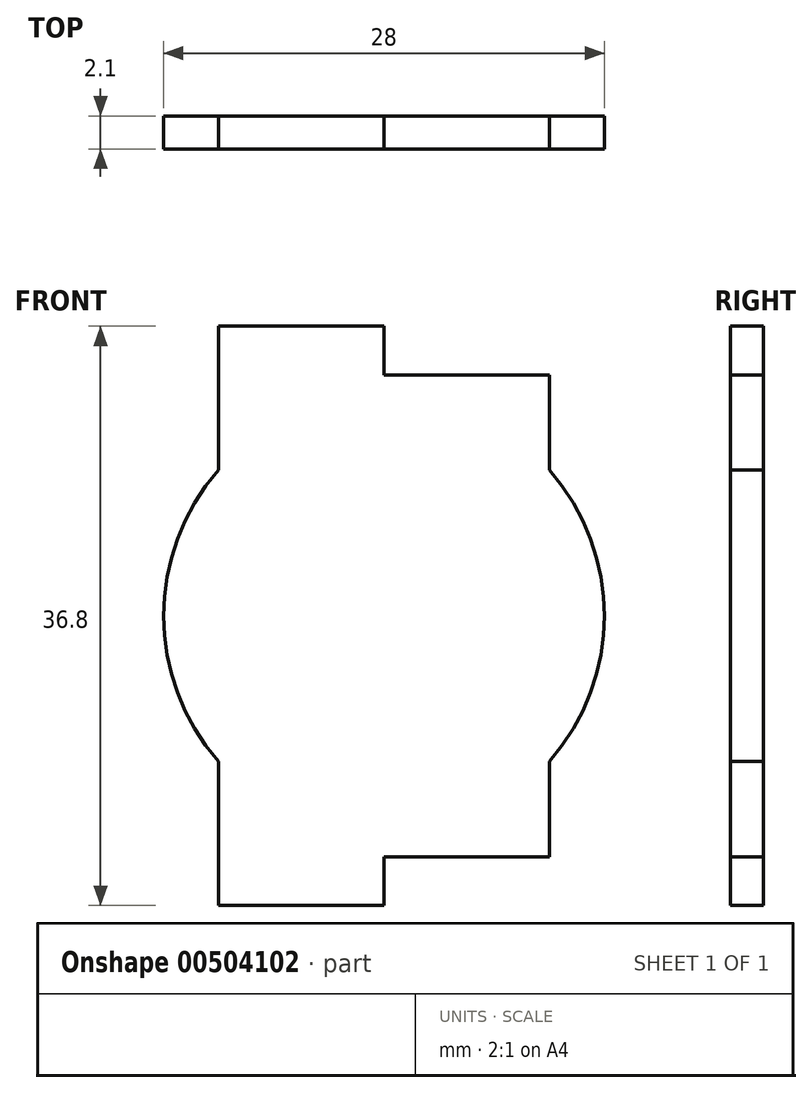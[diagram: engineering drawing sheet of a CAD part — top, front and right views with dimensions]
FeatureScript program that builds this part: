
annotation { "Feature Type Name" : "Feature", "Feature Type Description" : "" }
export const myFeature = defineFeature(function(context is Context, id is Id, definition is map)
    precondition{}
    {
        {
            var Q0;
            Q0=qCreatedBy(makeId("Front.planeOp"),FACE);
            var sketch = newSketch(context, id + "F0", { "sketchPlane" : qUnion([Q0])});
            skArc(sketch, "E0", {"start": v(-10.5, 9.26) * mm, "mid": v(-14, 0) * mm, "end": v(-10.5, -9.26) * mm});
            skLineSegment(sketch, "E1", {"start": v(-10.5, 9.26) * mm, "end": v(-10.5, 18.4) * mm});
            skLineSegment(sketch, "E2", {"start": v(-10.5, 18.4) * mm, "end": v(0, 18.4) * mm});
            skLineSegment(sketch, "E3", {"start": v(0, 18.4) * mm, "end": v(0, 15.3) * mm});
            skLineSegment(sketch, "E4", {"start": v(0, 15.3) * mm, "end": v(10.5, 15.3) * mm});
            skLineSegment(sketch, "E5", {"start": v(10.5, 15.3) * mm, "end": v(10.5, 9.26) * mm});
            skLineSegment(sketch, "E6", {"start": v(-10.5, -9.26) * mm, "end": v(-10.5, -18.4) * mm});
            skLineSegment(sketch, "E7", {"start": v(-10.5, -18.4) * mm, "end": v(0, -18.4) * mm});
            skLineSegment(sketch, "E8", {"start": v(0, -18.4) * mm, "end": v(0, -15.3) * mm});
            skLineSegment(sketch, "E9", {"start": v(0, -15.3) * mm, "end": v(10.5, -15.3) * mm});
            skLineSegment(sketch, "E10", {"start": v(10.5, -15.3) * mm, "end": v(10.5, -9.26) * mm});
            skArc(sketch, "E11.trimOffspring", {"start": v(10.5, -9.26) * mm, "mid": v(14, 0) * mm, "end": v(10.5, 9.26) * mm});
            skSolve(sketch);
        }
        {
            var Q0;
            Q0=makeQuery(id+"F0.imprint","IMPRINT",FACE,{"disambiguationData":[TD([[makeQuery(id+"F0.imprint","IMPRINT",EDGE,{"derivedFrom":sQuery(id+"F0.wireOp",EDGE,"E0")}),1.0]])]});
            extrude(context, id + "F1", {"entities" : qUnion([Q0]), "depth" : 2.1 * mm});
        }
    });
